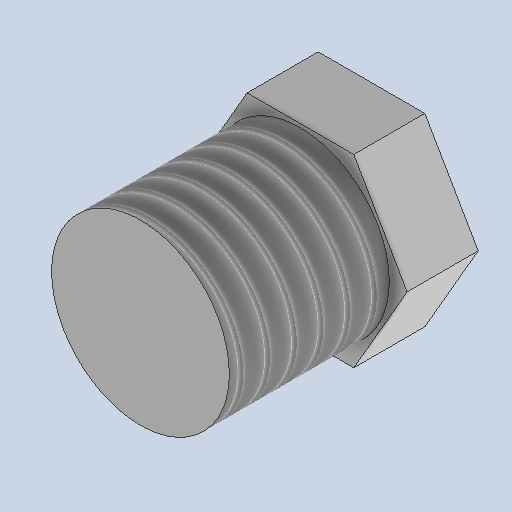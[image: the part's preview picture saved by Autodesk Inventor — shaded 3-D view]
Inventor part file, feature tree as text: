
AUTODESK INVENTOR PART (.ipt)
format: ipt  version: 2025.1 (Build 291241000, 241)  size: 156,672 bytes
history: native  units: mm
features: extrude x2, sketch x2, thread x1
ambient origin geometry x8: Origin, YZ Plane, XZ Plane, XY Plane, X Axis, Y Axis, Z Axis, Center Point
bodies: Volumenkörper1 (feature_tree)
feature tree (5):
  extrude  "Extrusion1"  Depth=10.0mm
  extrude  "Extrusion2"  Depth=13.0mm TaperAngle=0.0deg
  thread  "Gewinde1"  [1 undecoded]
  sketch  "Skizze1"  dims[d0=12.0mm d1=10.0mm]
  sketch  "Skizze2"  dims[d2=4.0mm d3=0.0mm d4=13.0mm d5=0.0mm d6=9.0mm d7=0.0mm]
note: 1 required parameter value undecoded (feature->parameter linkage not recoverable at this tier; creation-order binding heuristic only, values carry confidence <= 0.55)
